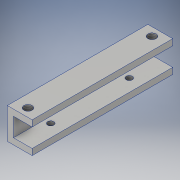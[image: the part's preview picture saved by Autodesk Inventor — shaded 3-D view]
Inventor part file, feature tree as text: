
AUTODESK INVENTOR PART (.ipt)
format: ipt  version: 2018 (Build 220112000, 112)  size: 137,728 bytes
history: native  units: in
note: dims shown in document units (in); Inventor stores cm internally (conversion verified against a paired STEP export)
features: thread x4, sketch x4, extrude x2, hole x2
ambient origin geometry x8: Origin, YZ Plane, XZ Plane, XY Plane, X Axis, Y Axis, Z Axis, Center Point
bodies: Solid1 (feature_tree)
feature tree (12):
  extrude  "Extrusion1"  Depth=2.6772in
  extrude  "Extrusion2"  Depth=0.5906in
  hole  "Hole1"  [1 undecoded]
  hole  "Hole2"  [1 undecoded]
  thread  "Thread1"  [1 undecoded]
  thread  "Thread2"  [1 undecoded]
  thread  "Thread3"  [1 undecoded]
  thread  "Thread4"  [1 undecoded]
  sketch  "Sketch1"  dims[d0=0.4724in d1=2.6772in]
  sketch  "Sketch2"  dims[d2=0.5906in d3=0.0in d4=0.1575in]
  sketch  "Sketch3"  dims[d5=0.1575in d6=0.2362in]
  sketch  "Sketch4"  dims[d7=0.2362in d8=0.1575in d9=0.1575in d10=0.1575in d11=0.328in d12=0.1575in d13=0.0787in d14=90.0deg d15=0.1181in d16=0.8108in d17=0.1181in d18=0.1181in d19=0.2362in d20=0.2362in d21=0.5906in d22=0.5906in d23=0.1181in d24=0.2362in d25=0.1575in d26=0.0787in d27=90.0deg d28=0.1181in d29=0.8108in d30=2.6772in d31=0.3543in d32=0.1181in d33=0.3543in d34=0.0in d35=0.3937in d36=0.0in d37=0.3937in d38=0.0in d39=0.3937in d40=0.0in d41=0.3937in d42=0.0in]
note: 6 required parameter values undecoded (feature->parameter linkage not recoverable at this tier; creation-order binding heuristic only, values carry confidence <= 0.55)
